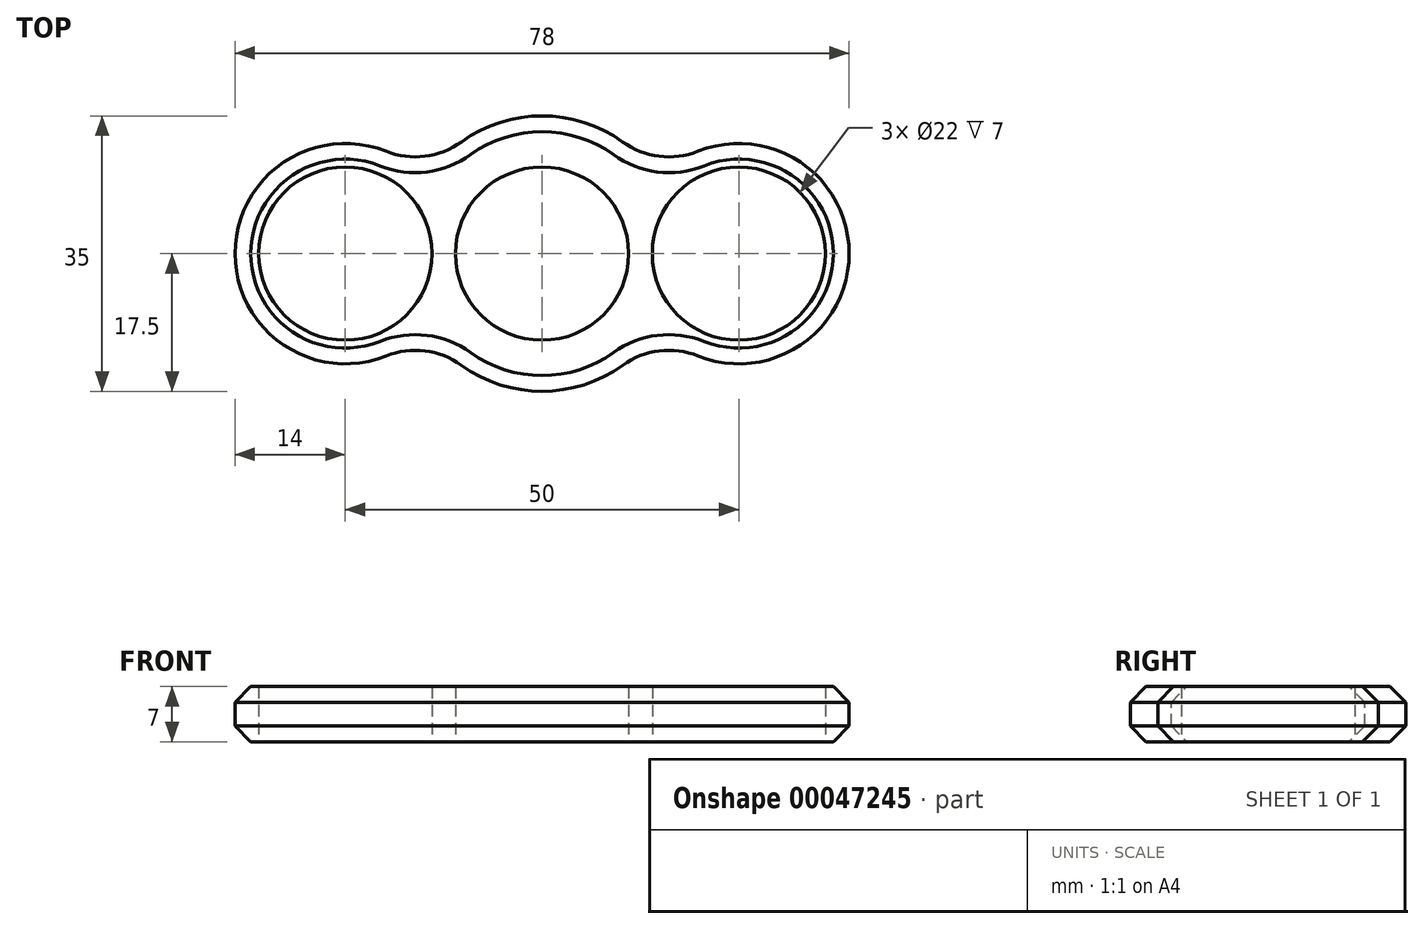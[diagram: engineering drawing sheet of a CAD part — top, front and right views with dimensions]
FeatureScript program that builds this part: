
annotation { "Feature Type Name" : "Feature", "Feature Type Description" : "" }
export const myFeature = defineFeature(function(context is Context, id is Id, definition is map)
    precondition{}
    {
        {
            var Q0;
            Q0=qCreatedBy(makeId("Top.planeOp"),FACE);
            var sketch = newSketch(context, id + "F0", { "sketchPlane" : qUnion([Q0])});
            skCircle(sketch, "E0", {"center": v(0, 0) * mm, "radius": 11 * mm});
            skLineSegment(sketch, "E1", {"start": v(0, 0) * mm, "end": v(25, 0) * mm, "construction": true});
            skCircle(sketch, "E2", {"center": v(25, 0) * mm, "radius": 11 * mm});
            skLineSegment(sketch, "E3", {"start": v(0, 0) * mm, "end": v(-25, 0) * mm, "construction": true});
            skCircle(sketch, "E4", {"center": v(-25, 0) * mm, "radius": 11 * mm});
            skArc(sketch, "E5", {"start": v(-14.7, 9.49) * mm, "mid": v(-39, 0) * mm, "end": v(-14.7, -9.49) * mm});
            skArc(sketch, "E6", {"start": v(14.7, -9.49) * mm, "mid": v(39, 0) * mm, "end": v(14.7, 9.49) * mm});
            skArc(sketch, "E7", {"start": v(-14.7, -9.49) * mm, "mid": v(0, -17.5) * mm, "end": v(14.7, -9.49) * mm});
            skArc(sketch, "E8.trimOffspring", {"start": v(14.7, 9.49) * mm, "mid": v(0, 17.5) * mm, "end": v(-14.7, 9.49) * mm});
            skSolve(sketch);
        }
        {
            var Q0;
            Q0 = qSketchRegion(id + "F0", true);
            extrude(context, id + "F1", {"entities" : qUnion([Q0]), "depth" : 7 * mm});
        }
        {
            var Q0;
            Q0=makeQuery(id+"F1.opExtrude","SWEPT_EDGE",EDGE,{"disambiguationData":[OSD([sQuery(id+"F0.wireOp",EDGE,"E5"),sQuery(id+"F0.wireOp",EDGE,"E7")])]});
            var Q1;
            Q1=makeQuery(id+"F1.opExtrude","SWEPT_EDGE",EDGE,{"disambiguationData":[OSD([sQuery(id+"F0.wireOp",EDGE,"E6"),sQuery(id+"F0.wireOp",EDGE,"E7")])]});
            var Q2;
            Q2=makeQuery(id+"F1.opExtrude","SWEPT_EDGE",EDGE,{"disambiguationData":[OSD([sQuery(id+"F0.wireOp",EDGE,"E5"),sQuery(id+"F0.wireOp",EDGE,"E8.trimOffspring")])]});
            var Q3;
            Q3=makeQuery(id+"F1.opExtrude","SWEPT_EDGE",EDGE,{"disambiguationData":[OSD([sQuery(id+"F0.wireOp",EDGE,"E6"),sQuery(id+"F0.wireOp",EDGE,"E8.trimOffspring")])]});
            fillet(context, id + "F2", {"entities" : qUnion([Q0, Q1, Q2, Q3]), "radius" : 10 * mm, "tangentPropagation" : true, "allowEdgeOverflow" : false});
        }
        {
            var Q0;
            Q0=makeQuery(id+"F1.opExtrude","CAP_EDGE",EDGE,{"disambiguationData":[OSD([sQuery(id+"F0.wireOp",EDGE,"E5")])],"isStart":false});
            chamfer(context, id + "F3", {"entities" : qUnion([Q0]), "width" : 2 * mm, "tangentPropagation" : true});
        }
        {
            var Q0;
            Q0=makeQuery(id+"F1.opExtrude","CAP_EDGE",EDGE,{"disambiguationData":[OSD([sQuery(id+"F0.wireOp",EDGE,"E5")])],"isStart":true});
            chamfer(context, id + "F4", {"entities" : qUnion([Q0]), "width" : 2 * mm, "tangentPropagation" : true});
        }
    });
